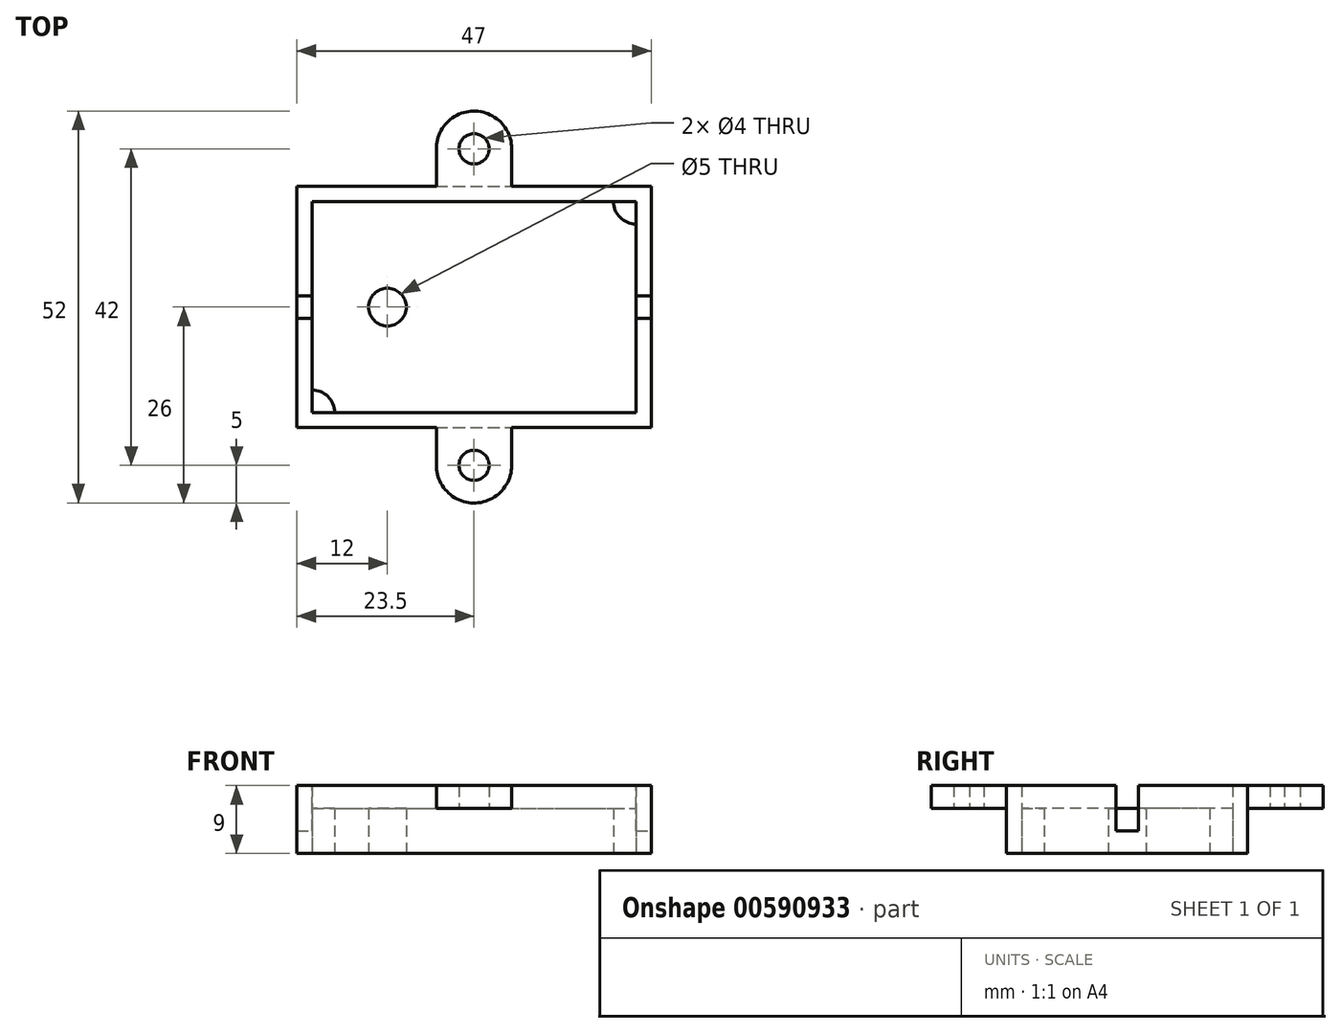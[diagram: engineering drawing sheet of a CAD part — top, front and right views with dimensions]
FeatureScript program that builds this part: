
annotation { "Feature Type Name" : "Feature", "Feature Type Description" : "" }
export const myFeature = defineFeature(function(context is Context, id is Id, definition is map)
    precondition{}
    {
        {
            var Q0;
            Q0=qCreatedBy(makeId("Top.planeOp"),FACE);
            var sketch = newSketch(context, id + "F0", { "sketchPlane" : qUnion([Q0])});
            skLineSegment(sketch, "E0.bottom", {"start": v(-23.5, 16) * mm, "end": v(23.5, 16) * mm});
            skLineSegment(sketch, "E0.top", {"start": v(-23.5, -16) * mm, "end": v(23.5, -16) * mm});
            skLineSegment(sketch, "E0.left", {"start": v(-23.5, 16) * mm, "end": v(-23.5, -16) * mm});
            skLineSegment(sketch, "E0.right", {"start": v(23.5, 16) * mm, "end": v(23.5, -16) * mm});
            skPoint(sketch, "E0.middle", {"position": v(0, 0) * mm});
            skLineSegment(sketch, "E1.0", {"start": v(-21.5, 14) * mm, "end": v(21.5, 14) * mm});
            skLineSegment(sketch, "E1.1", {"start": v(-21.5, 14) * mm, "end": v(-21.5, -14) * mm});
            skLineSegment(sketch, "E1.2", {"start": v(-21.5, -14) * mm, "end": v(21.5, -14) * mm});
            skLineSegment(sketch, "E1.3", {"start": v(21.5, 14) * mm, "end": v(21.5, -14) * mm});
            skCircle(sketch, "E2", {"center": v(-11.5, 0) * mm, "radius": 2.5 * mm});
            skArc(sketch, "E3", {"start": v(21.5, 11) * mm, "mid": v(19.38, 11.88) * mm, "end": v(18.5, 14) * mm});
            skArc(sketch, "E4.MirrorCS", {"start": v(21.5, -11) * mm, "mid": v(19.38, -11.88) * mm, "end": v(18.5, -14) * mm});
            skArc(sketch, "E5.MirrorCS", {"start": v(-21.5, 11) * mm, "mid": v(-19.38, 11.88) * mm, "end": v(-18.5, 14) * mm});
            skArc(sketch, "E6.MirrorCS", {"start": v(-21.5, -11) * mm, "mid": v(-19.38, -11.88) * mm, "end": v(-18.5, -14) * mm});
            skCircle(sketch, "E7", {"center": v(0, 21) * mm, "radius": 2 * mm});
            skArc(sketch, "E8", {"start": v(5, 20.97) * mm, "mid": v(-0.05, 26) * mm, "end": v(-5, 20.87) * mm});
            skLineSegment(sketch, "E9", {"start": v(5, 21.03) * mm, "end": v(5, 16) * mm});
            skLineSegment(sketch, "E10", {"start": v(-5, 20.87) * mm, "end": v(-5, 16) * mm});
            skLineSegment(sketch, "E11.MirrorCS", {"start": v(-5, -20.87) * mm, "end": v(-5, -16) * mm});
            skLineSegment(sketch, "E12.MirrorCS", {"start": v(5, -21.03) * mm, "end": v(5, -16) * mm});
            skCircle(sketch, "E13.MirrorC", {"center": v(0, -21) * mm, "radius": 2 * mm});
            skArc(sketch, "E14.MirrorCS", {"start": v(5, -20.97) * mm, "mid": v(-0.05, -26) * mm, "end": v(-5, -20.87) * mm});
            skSolve(sketch);
        }
        {
            var Q0;
            {var subQ8=sQuery(id+"F0.wireOp",EDGE,"E0.left");Q0=makeQuery(id+"F0.imprint","IMPRINT",FACE,{"disambiguationData":[TD([[makeQuery(id+"F0.imprint","IMPRINT",EDGE,{"derivedFrom":subQ8}),1.0]])]});}
            extrude(context, id + "F1", {"entities" : qUnion([Q0]), "depth" : 9 * mm, "offsetDistance" : 25 * mm});
        }
        {
            var Q0;
            Q0=makeQuery(id+"F0.imprint","IMPRINT",FACE,{"disambiguationData":[TD([[makeQuery(id+"F0.imprint","IMPRINT",EDGE,{"derivedFrom":sQuery(id+"F0.wireOp",EDGE,"E2")}),-1.0]])]});
            extrude(context, id + "F2", {"entities" : qUnion([Q0]), "operationType" : NewBodyOperationType.ADD, "depth" : 2 * mm, "offsetDistance" : 25 * mm});
        }
        {
            var Q0;
            {var subQ3=sQuery(id+"F0.wireOp",EDGE,"E5.MirrorCS");Q0=makeQuery(id+"F0.imprint","IMPRINT",FACE,{"disambiguationData":[TD([[makeQuery(id+"F0.imprint","IMPRINT",EDGE,{"derivedFrom":subQ3}),1.0]])]});}
            var Q1;
            {var subQ3=sQuery(id+"F0.wireOp",EDGE,"E3");Q1=makeQuery(id+"F0.imprint","IMPRINT",FACE,{"disambiguationData":[TD([[makeQuery(id+"F0.imprint","IMPRINT",EDGE,{"derivedFrom":subQ3}),-1.0]])]});}
            var Q2;
            {var subQ3=sQuery(id+"F0.wireOp",EDGE,"E4.MirrorCS");Q2=makeQuery(id+"F0.imprint","IMPRINT",FACE,{"disambiguationData":[TD([[makeQuery(id+"F0.imprint","IMPRINT",EDGE,{"derivedFrom":subQ3}),1.0]])]});}
            var Q3;
            {var subQ3=sQuery(id+"F0.wireOp",EDGE,"E6.MirrorCS");Q3=makeQuery(id+"F0.imprint","IMPRINT",FACE,{"disambiguationData":[TD([[makeQuery(id+"F0.imprint","IMPRINT",EDGE,{"derivedFrom":subQ3}),-1.0]])]});}
            extrude(context, id + "F3", {"entities" : qUnion([Q0, Q1, Q2, Q3]), "operationType" : NewBodyOperationType.ADD, "depth" : 6 * mm, "offsetDistance" : 25 * mm});
        }
        {
            var Q0;
            Q0=makeQuery(id+"F0.imprint","IMPRINT",FACE,{"disambiguationData":[TD([[makeQuery(id+"F0.imprint","IMPRINT",EDGE,{"derivedFrom":sQuery(id+"F0.wireOp",EDGE,"E7")}),-1.0]])]});
            var Q1;
            {var subQ1=sQuery(id+"F0.wireOp",EDGE,"E11.MirrorCS");Q1=makeQuery(id+"F0.imprint","IMPRINT",FACE,{"disambiguationData":[TD([[makeQuery(id+"F0.imprint","IMPRINT",EDGE,{"derivedFrom":subQ1}),-1.0]])]});}
            extrude(context, id + "F4", {"entities" : qUnion([Q0, Q1]), "operationType" : NewBodyOperationType.ADD, "depth" : 9 * mm, "offsetDistance" : 25 * mm, "hasSecondDirection" : true, "secondDirectionOppositeDirection" : false, "secondDirectionDepth" : 6 * mm});
        }
        {
            var Q0;
            {var subQ0=sQuery(id+"F0.wireOp",EDGE,"E0.top");var subQ1=sQuery(id+"F0.wireOp",EDGE,"E0.bottom");Q0=makeQuery(id+"F4.boolean.opBoolean","MERGE",FACE,{"derivedFrom":[makeQuery(id+"F1.opExtrude","CAP_FACE",FACE,{"disambiguationData":[OSD([subQ1,subQ0,sQuery(id+"F0.wireOp",EDGE,"E0.left"),sQuery(id+"F0.wireOp",EDGE,"E0.right"),sQuery(id+"F0.wireOp",EDGE,"E1.0"),sQuery(id+"F0.wireOp",EDGE,"E1.1"),sQuery(id+"F0.wireOp",EDGE,"E1.2"),sQuery(id+"F0.wireOp",EDGE,"E1.3")])],"isStart":false}),makeQuery(id+"F4.opExtrude","CAP_FACE",FACE,{"disambiguationData":[OSD([subQ1,sQuery(id+"F0.wireOp",EDGE,"E7"),sQuery(id+"F0.wireOp",EDGE,"E8"),sQuery(id+"F0.wireOp",EDGE,"E9"),sQuery(id+"F0.wireOp",EDGE,"E10")])],"isStart":false}),makeQuery(id+"F4.opExtrude","CAP_FACE",FACE,{"disambiguationData":[OSD([subQ0,sQuery(id+"F0.wireOp",EDGE,"E11.MirrorCS"),sQuery(id+"F0.wireOp",EDGE,"E12.MirrorCS"),sQuery(id+"F0.wireOp",EDGE,"E13.MirrorC"),sQuery(id+"F0.wireOp",EDGE,"E14.MirrorCS")])],"isStart":false})]});}
            var sketch = newSketch(context, id + "F5", { "sketchPlane" : qUnion([Q0])});
            skLineSegment(sketch, "E15.bottom", {"start": v(-27.5, 1.5) * mm, "end": v(27.5, 1.5) * mm});
            skLineSegment(sketch, "E15.top", {"start": v(-27.5, -1.5) * mm, "end": v(27.5, -1.5) * mm});
            skLineSegment(sketch, "E15.left", {"start": v(-27.5, 1.5) * mm, "end": v(-27.5, -1.5) * mm});
            skLineSegment(sketch, "E15.right", {"start": v(27.5, 1.5) * mm, "end": v(27.5, -1.5) * mm});
            skPoint(sketch, "E15.middle", {"position": v(0, 0) * mm});
            skSolve(sketch);
        }
        {
            var Q0;
            {var subQ0=sQuery(id+"F5.wireOp",EDGE,"E15.bottom");var subQ1=makeQuery(id+"F1.opExtrude","CAP_EDGE",EDGE,{"disambiguationData":[OSD([sQuery(id+"F0.wireOp",EDGE,"E0.left")])],"isStart":false});var subQ2=makeQuery(id+"F5.imprint","INTERSECT",VERTEX,{"derivedFrom":[subQ1,subQ0]});Q0=makeQuery(id+"F5.imprint","IMPRINT",FACE,{"disambiguationData":[TD([[makeQuery(id+"F5.imprint","IMPRINT",EDGE,{"disambiguationData":[TD([[subQ2,-1.0]])],"derivedFrom":subQ0}),-1.0]])]});}
            var Q1;
            {var subQ0=sQuery(id+"F5.wireOp",EDGE,"E15.bottom");var subQ1=makeQuery(id+"F1.opExtrude","CAP_EDGE",EDGE,{"disambiguationData":[OSD([sQuery(id+"F0.wireOp",EDGE,"E0.right")])],"isStart":false});var subQ2=makeQuery(id+"F5.imprint","INTERSECT",VERTEX,{"derivedFrom":[subQ1,subQ0]});Q1=makeQuery(id+"F5.imprint","IMPRINT",FACE,{"disambiguationData":[TD([[makeQuery(id+"F5.imprint","IMPRINT",EDGE,{"disambiguationData":[TD([[subQ2,1.0]])],"derivedFrom":subQ0}),-1.0]])]});}
            extrude(context, id + "F6", {"entities" : qUnion([Q0, Q1]), "operationType" : NewBodyOperationType.REMOVE, "oppositeDirection" : true, "depth" : 6 * mm, "offsetDistance" : 25 * mm});
        }
    });
